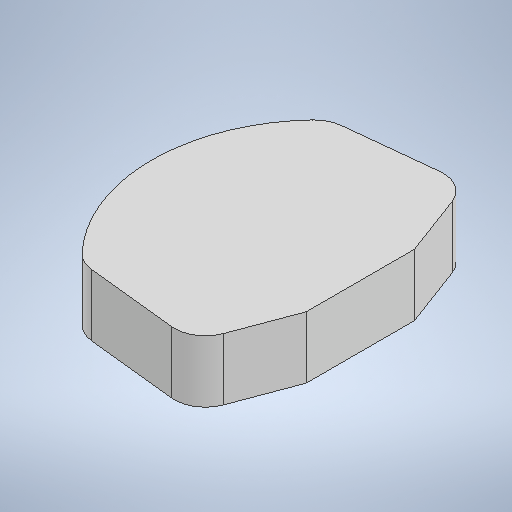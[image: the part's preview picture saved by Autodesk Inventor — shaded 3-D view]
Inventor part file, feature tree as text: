
AUTODESK INVENTOR PART (.ipt)
format: ipt  version: 2025.2 (Build 292293000, 293)  size: 216,064 bytes
history: native  units: in
note: dims shown in document units (in); Inventor stores cm internally (conversion verified against a paired STEP export)
features: extrude x1, fillet x1, sketch x1
ambient origin geometry x8: Origin, YZ Plane, XZ Plane, XY Plane, X Axis, Y Axis, Z Axis, Center Point
bodies: Solid1 (feature_tree)
feature tree (3):
  extrude  "Extrusion1"  Depth=0.1378in
  fillet  "Fillet1"  Radius=0.2106in
  sketch  "Sketch1"  dims[d0=0.2756in d1=0.1378in d2=0.2106in d3=0.0787in d4=0.2106in d5=0.0787in d6=0.315in d7=0.315in d8=0.1772in d9=0.1772in d10=0.5315in d11=0.1575in d12=0.0in d13=0.0787in]
